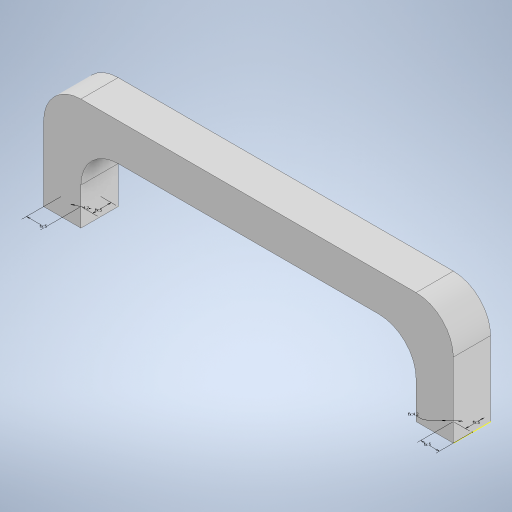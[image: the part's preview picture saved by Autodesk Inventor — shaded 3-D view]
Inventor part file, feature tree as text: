
AUTODESK INVENTOR PART (.ipt)
format: ipt  version: 2023 (Build 270158000, 158)  size: 246,272 bytes
history: native  units: in
note: dims shown in document units (in); Inventor stores cm internally (conversion verified against a paired STEP export)
features: sketch x2, extrude x1, fillet x1
ambient origin geometry x8: Origin, YZ Plane, XZ Plane, XY Plane, X Axis, Y Axis, Z Axis, Center Point
bodies: Solid1 (feature_tree)
feature tree (4):
  extrude  "Extrusion1"  Depth=1.1811in
  fillet  "Fillet1"  Radius=0.3937in
  sketch  "Sketch2"  dims[d3=0.3937in d4=0.3937in d5=0.3937in d6=0.0in d7=0.3937in d8=0.1969in d9=0.1969in d10=0.1654in d11=0.1969in d12=0.1969in d13=0.1654in]
  sketch  "Sketch1"  dims[d0=4.3307in d1=1.1811in d2=0.3937in]
